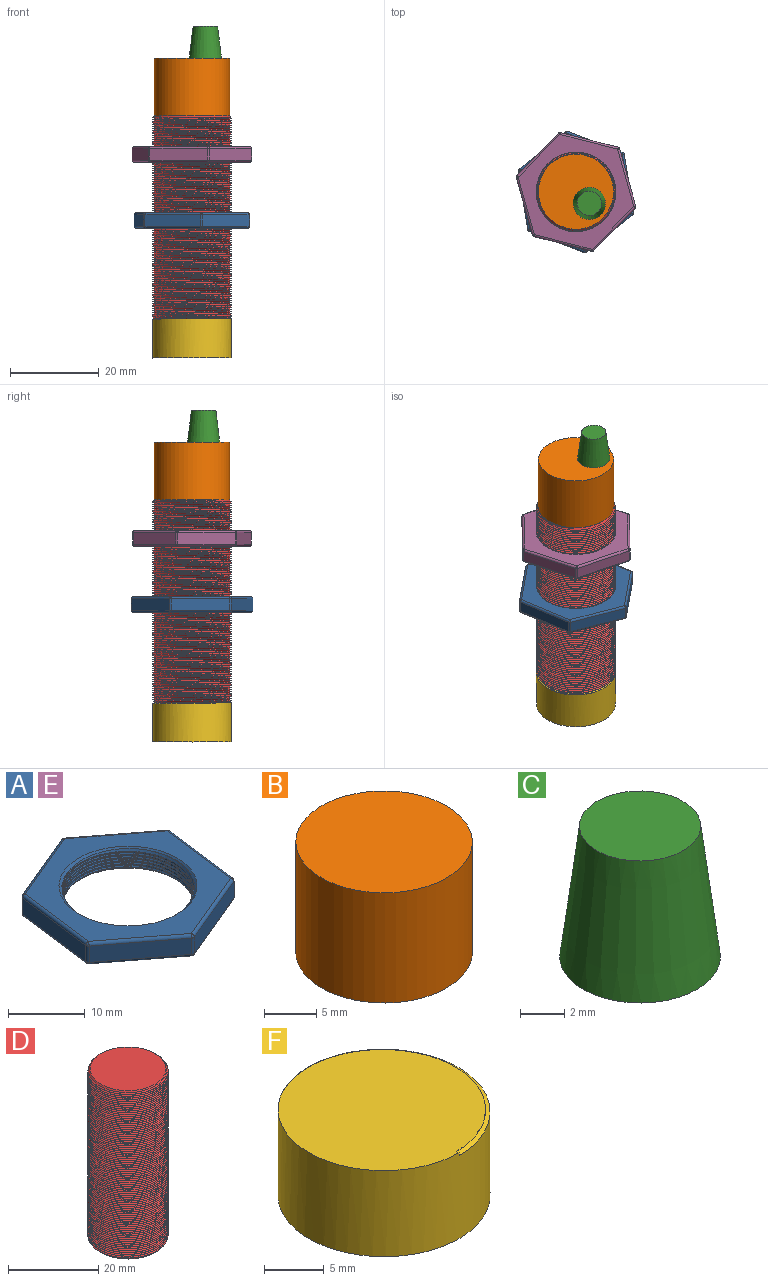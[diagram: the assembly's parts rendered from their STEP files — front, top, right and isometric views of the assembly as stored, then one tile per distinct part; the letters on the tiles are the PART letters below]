
ASSEMBLY  parts=6 mates=5
PART A: 44 faces, bbox 25.7x27.6x3.7 mm
  f0: cone r=8.97mm half-angle=45deg, axis (0,0,-1), area 28.1mm2, adj f7,f10,f41,f42,f43
  f1: cone r=8.47mm half-angle=45deg, axis (0,0,1), area 28.2mm2, adj f7,f9,f41,f42,f43
  f2: plane 10.69x8.17mm, normal (0.61,0.79,0), area 34.8mm2, adj f29,f34,f37,f40
  f3: plane 12.42x5.18mm, normal (-0.38,0.92,0), area 34.8mm2, adj f26,f35,f36,f40
  f4: plane 13.34x2.59mm, normal (-0.99,0.13,0), area 34.8mm2, adj f16,f25,f26,f27
  f5: plane 10.69x8.17mm, normal (-0.61,-0.79,0), area 34.8mm2, adj f11,f15,f16,f17
  f6: plane 12.42x5.18mm, normal (0.38,-0.92,0), area 34.8mm2, adj f11,f14,f18,f19
  f7: cylinder r=8.47mm len=16.95mm, axis (0,0,-1), area 66.1mm2, adj f0,f1,f42,f43
  f8: plane 13.34x2.59mm, normal (0.99,-0.13,0), area 34.8mm2, adj f19,f24,f28,f29
  f9: plane 26.69x24.84mm, normal (0,0,1), area 217.3mm2, adj f1,f14,f15,f24,f25,f34,f35
  f10: plane 26.69x24.84mm, normal (0,0,-1), area 217.3mm2, adj f0,f17,f18,f27,f28,f36,f37
  f11: cylinder r=0.45mm len=2.59mm, axis (0,0,-1), area 1.2mm2, adj f5,f6,f12,f13
  f12: sphere r=0.45mm, area 0.2mm2, adj f11,f14,f15
  f13: sphere r=0.45mm, area 0.1mm2, adj f11,f17,f18
  f14: cylinder r=0.45mm len=12.59mm, axis (-0.92,-0.38,0), area 9.4mm2, adj f6,f9,f12,f20
  f15: cylinder r=0.45mm len=10.96mm, axis (-0.79,0.61,0), area 9.4mm2, adj f5,f9,f12,f21
  f16: cylinder r=0.45mm len=2.59mm, axis (0,0,-1), area 1.2mm2, adj f4,f5,f21,f22
  f17: cylinder r=0.45mm len=10.96mm, axis (0.79,-0.61,0), area 9.4mm2, adj f5,f10,f13,f22
  f18: cylinder r=0.45mm len=12.59mm, axis (0.92,0.38,0), area 9.4mm2, adj f6,f10,f13,f23
  f19: cylinder r=0.45mm len=2.59mm, axis (0,0,-1), area 1.2mm2, adj f6,f8,f20,f23
  f20: sphere r=0.45mm, area 0.2mm2, adj f14,f19,f24
  f21: sphere r=0.45mm, area 0.2mm2, adj f15,f16,f25
  f22: sphere r=0.45mm, area 0.2mm2, adj f16,f17,f27
  f23: sphere r=0.45mm, area 0.2mm2, adj f18,f19,f28
  f24: cylinder r=0.45mm len=13.4mm, axis (-0.13,-0.99,0), area 9.4mm2, adj f8,f9,f20,f30
  f25: cylinder r=0.45mm len=13.4mm, axis (0.13,0.99,0), area 9.4mm2, adj f4,f9,f21,f31
  f26: cylinder r=0.45mm len=2.59mm, axis (0,0,-1), area 1.2mm2, adj f3,f4,f31,f32
  f27: cylinder r=0.45mm len=13.4mm, axis (-0.13,-0.99,0), area 9.4mm2, adj f4,f10,f22,f32
  f28: cylinder r=0.45mm len=13.4mm, axis (0.13,0.99,0), area 9.4mm2, adj f8,f10,f23,f33
  f29: cylinder r=0.45mm len=2.59mm, axis (0,0,-1), area 1.2mm2, adj f2,f8,f30,f33
  f30: sphere r=0.45mm, area 0.2mm2, adj f24,f29,f34
  f31: sphere r=0.45mm, area 0.2mm2, adj f25,f26,f35
  f32: sphere r=0.45mm, area 0.2mm2, adj f26,f27,f36
  f33: sphere r=0.45mm, area 0.1mm2, adj f28,f29,f37
  f34: cylinder r=0.45mm len=10.96mm, axis (0.79,-0.61,0), area 9.4mm2, adj f2,f9,f30,f38
  f35: cylinder r=0.45mm len=12.59mm, axis (0.92,0.38,0), area 9.4mm2, adj f3,f9,f31,f38
  f36: cylinder r=0.45mm len=12.59mm, axis (-0.92,-0.38,0), area 9.4mm2, adj f3,f10,f32,f39
  f37: cylinder r=0.45mm len=10.96mm, axis (-0.79,0.61,0), area 9.4mm2, adj f2,f10,f33,f39
  f38: sphere r=0.45mm, area 0.4mm2, adj f34,f35,f40
  f39: sphere r=0.45mm, area 0.3mm2, adj f36,f37,f40
  f40: cylinder r=0.45mm len=2.59mm, axis (0,0,-1), area 1.2mm2, adj f2,f3,f38,f39
  f41: bspline ~20.28x17.56mm, area 140.5mm2, adj f0,f1,f42,f43
  f42: bspline ~19.76x17.11mm, area 44.2mm2, adj f0,f1,f7,f41
  f43: bspline ~20.28x17.56mm, area 92.2mm2, adj f0,f1,f7,f41
PART B: 3 faces, bbox 17x17x13 mm
  f0: cylinder r=8.47mm len=16.95mm, axis (0,0,-1), area 689.6mm2, adj f1,f2
  f1: plane 16.95x16.95mm, normal (0,0,1), area 225.6mm2, adj f0
  f2: plane 16.95x16.95mm, normal (0,0,-1), area 225.6mm2, adj f0
PART C: 3 faces, bbox 7.3x7.3x7.3 mm
  f0: cone r=3.65mm half-angle=7deg, axis (0,0,-1), area 147mm2, adj f1,f2
  f1: plane 5.51x5.51mm, normal (0,0,1), area 23.8mm2, adj f0
  f2: plane 7.29x7.29mm, normal (0,0,-1), area 41.7mm2, adj f0
PART D: 8 faces, bbox 20.6x17.8x46 mm
  f0: cone r=8.41mm half-angle=45deg, axis (0,0,-1), area 24.3mm2, adj f1,f4,f6,f7
  f1: cone r=8.41mm half-angle=45deg, axis (0,0,-1), area 0.5mm2, adj f0,f3,f7
  f2: cone r=8.91mm half-angle=45deg, axis (0,0,1), area 24.8mm2, adj f3,f5,f6,f7
  f3: cylinder r=8.91mm len=44.78mm, axis (0,0,-1), area 68.7mm2, adj f1,f2,f6,f7
  f4: plane 16.82x16.82mm, normal (0,0,1), area 222.2mm2, adj f0
  f5: plane 16.82x16.82mm, normal (0,0,-1), area 222.2mm2, adj f2
  f6: bspline ~45.81x20.58mm, area 2210.6mm2, adj f0,f2,f3,f7
  f7: bspline ~45.81x20.58mm, area 2224.2mm2, adj f0,f1,f2,f3,f6
PART E: same geometry as A
PART F: 6 faces, bbox 19.6x18.2x9.5 mm
  f0: cylinder r=8.91mm len=17.82mm, axis (0,0,1), area 490.6mm2, adj f1,f2,f3,f5
  f1: plane 18.14x17.92mm, normal (0,0,1), area 242mm2, adj f0,f3,f4,f5
  f2: plane 17.82x17.82mm, normal (0,0,-1), area 249.4mm2, adj f0
  f3: plane 0.39x0.3mm, normal (1,0,0), area 0.1mm2, adj f0,f1,f4,f5
  f4: bspline ~7.72x4.65mm, area 0.5mm2, adj f1,f3,f5
  f5: bspline ~18x17.82mm, area 9mm2, adj f0,f1,f3,f4
PLACE A rot(axis=(0,0,1),76.5deg) t=(-36.34,-8.78,7.99)mm
PLACE B rot(axis=(0,0,1),138.8deg) t=(-36.34,-8.78,-12.4)mm
PLACE C rot(axis=(0,0,1),138.8deg) t=(-36.36,-14.89,-12.4)mm
PLACE D rot(axis=(0,0,1),138.8deg) t=(-36.34,-8.78,-12.4)mm
PLACE E rot(axis=(0,0,1),83.1deg) t=(-36.34,-8.78,22.9)mm
PLACE F rot(axis=(0,0,1),138.8deg) t=(-36.34,-8.78,-12.4)mm
MATE cylindrical E.f0 <-> B.f0  axis (0,0,-1) through (-36.34,-8.78,22.9)mm
MATE fastened D.f0 <-> F.f0  axis (0,0,-1) through (-36.34,-8.78,-12.4)mm
MATE cylindrical A.f0 <-> B.f0  axis (0,0,-1) through (-36.34,-8.78,7.99)mm
MATE fastened C.f0 <-> B.f1  axis (0,0,-1) through (-33.33,-11.42,46.33)mm
MATE fastened B.f0 <-> D.f0  axis (0,0,-1) through (-36.34,-8.78,33.38)mm
